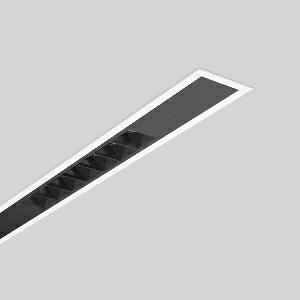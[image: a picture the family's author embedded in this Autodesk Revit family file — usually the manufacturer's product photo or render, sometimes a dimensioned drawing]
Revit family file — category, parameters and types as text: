
# Revit family: less_is_more_beamline_312477_002_6643
name_source: partatom
category: Lighting Fixtures
units: mm (PartAtom-declared; Revit-internal decimal feet)

## family parameters
Cut with Voids When Loaded = No
Host = Face
Light Source = No
Part Type = Normal
Room Calculation Point = No
Round Connector Dimension = Use Diameter
Shared = No

## types (1)
- LESS IS MORE BEAMLINE (1 x LED Modul 930, 1012.5 lm, 3000)
    Apparent Load = 47 VA
    CIE Flux Codes = 100 100 100 100 100
    Color Rendering = 90
    Color Temperature = 3000
    Default Elevation = 1800 mm
    Description = Series: LESS IS MORE BEAMLINE
Linear recessed ceiling and wall luminaire for aesthetically sophisticated lighting. Luminaire with four LED light units. Housing: extruded aluminium profile, powder-coated. End cap aluminium powder-coated. LED light unit with MRS technology: Mini-Reflector-System made of metallised thermoplastic with prismatic black glare-suppressing frame for pleasant glare-free light (RUG < 10). Each LED light unit has 7 reflector elements. Narrow beam light distribution. Ceiling installation with pre-assembled SBS mounting system. LED unit with integrated converter interchangeable and removable. Suitable for through-wiring. 
Colour: traffic white, matt (RAL 9016)
Length: 2262 mm
Width: 71 mm
Height: 1.5 mm
Cut-out length: 2243 mm
Cut-out width: 60 mm
Recess height: 125 mm
Luminaire: recess height: 106 mm
Lamp: LED
Socket: without socket
Colour temperature: 3000K
Colour rendering index (CRI): 90
System power: 47 W
Rated luminous flux: 4050 lm
Luminous efficiency: 86 lm/W
Control gear: Regulated power supply
Protection class: I
Type of protection: IP 20
    Height = 0 mm  [stored 0 ft]
    Lamp = 1 x LED Modul 930
    Lamp Light Flux = 1012.5 lm
    Lamp count = 1
    Length = 2262 mm
    Lifetime = 50000 h
    Luminous efficacy = 86 lm/W
    Manufacturer = RZB
    ModVariant = No
    Model = 312477.002
    Mounting Place = Ceiling, Wall
    Mounting Type = Recessed
    Number of Poles = 1
    OnlyDefault = Yes
    Power Factor = 1
    Product Name = LESS IS MORE BEAMLINE
    Product group = Recessed LED linear luminaires
    ProductGroupID = 407
    Protection Class = Protection class I
    Protection Degree = IP 20
    RLX_Detail_Level = 1
    RLX_Emergency_Light_Flux = 0 lm
    RLX_Emergency_Type = 0
    RLX_Emergency_Type_DB = No
    RlxData = <blob elided: 24409 chars, md5=f565cc48>
    Socket = socket
    Standby Power = 0 W
    System Light Flux = 4050 lm
    System Power = 47 W
    Type Comments = Product without accessories
    Type Image = 312465.002.jpg
    URL = http://relux.com
    VarID = ---
    Voltage = 230 V
    Voltage Range = 220-240 V
    Weight = 0.00 kg
    Width = 71 mm

note: [stored X ft] marks values corroborated as IEEE doubles in the binary element streams (Revit-internal decimal feet)

## geometry (parser evidence)
native form markers: Blend x4, Sweep x18
no freeform markers — native parametric forms only
